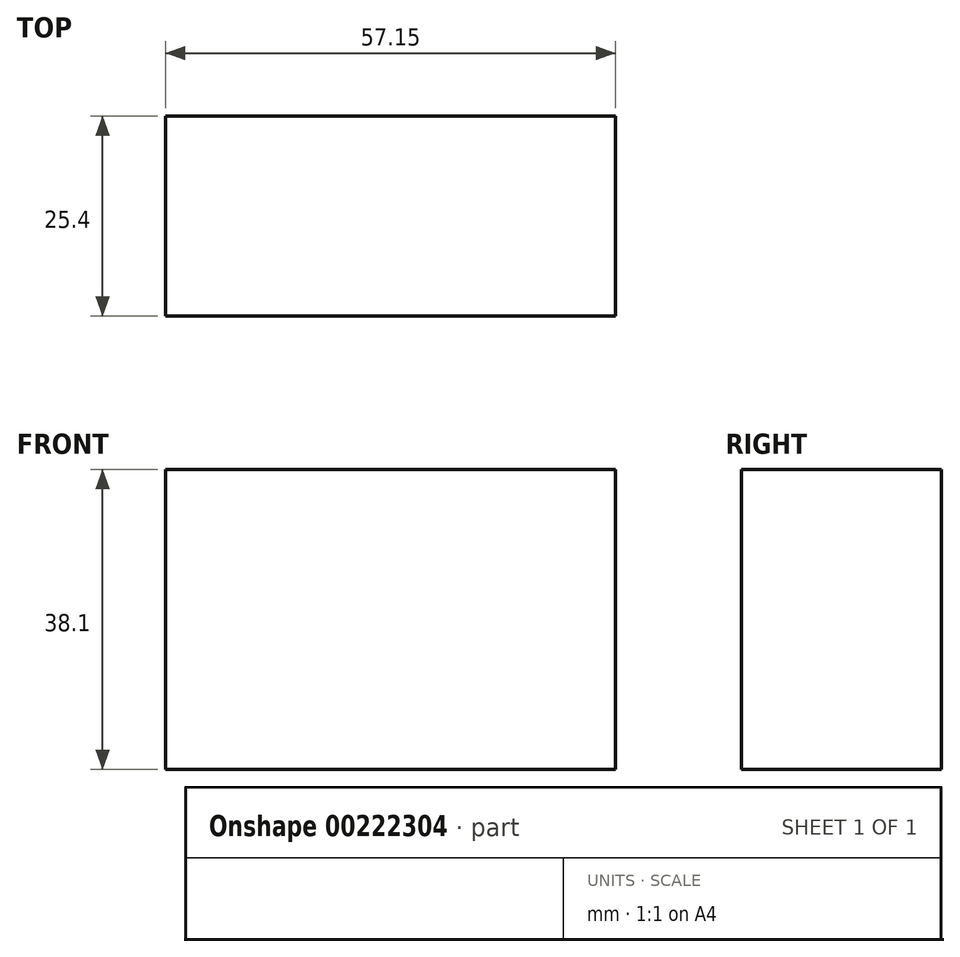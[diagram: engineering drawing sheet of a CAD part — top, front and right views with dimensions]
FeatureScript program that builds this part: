
annotation { "Feature Type Name" : "Feature", "Feature Type Description" : "" }
export const myFeature = defineFeature(function(context is Context, id is Id, definition is map)
    precondition{}
    {
        {
            var Q0;
            Q0=qCreatedBy(makeId("Front.planeOp"),FACE);
            var sketch = newSketch(context, id + "F0", { "sketchPlane" : qUnion([Q0])});
            skLineSegment(sketch, "E0.bottom", {"start": v(-24.1, 24.92) * mm, "end": v(-81.25, 24.92) * mm});
            skLineSegment(sketch, "E0.top", {"start": v(-24.1, 63.02) * mm, "end": v(-81.25, 63.02) * mm});
            skLineSegment(sketch, "E0.left", {"start": v(-24.1, 24.92) * mm, "end": v(-24.1, 63.02) * mm});
            skLineSegment(sketch, "E0.right", {"start": v(-81.25, 24.92) * mm, "end": v(-81.25, 63.02) * mm});
            skPoint(sketch, "E0.middle", {"position": v(-52.68, 43.97) * mm});
            skSolve(sketch);
        }
        {
            var Q0;
            Q0 = qSketchRegion(id + "F0", true);
            extrude(context, id + "F1", {"entities" : qUnion([Q0]), "endBound" : BoundingType.SYMMETRIC, "depth" : 25.4 * mm});
        }
    });
